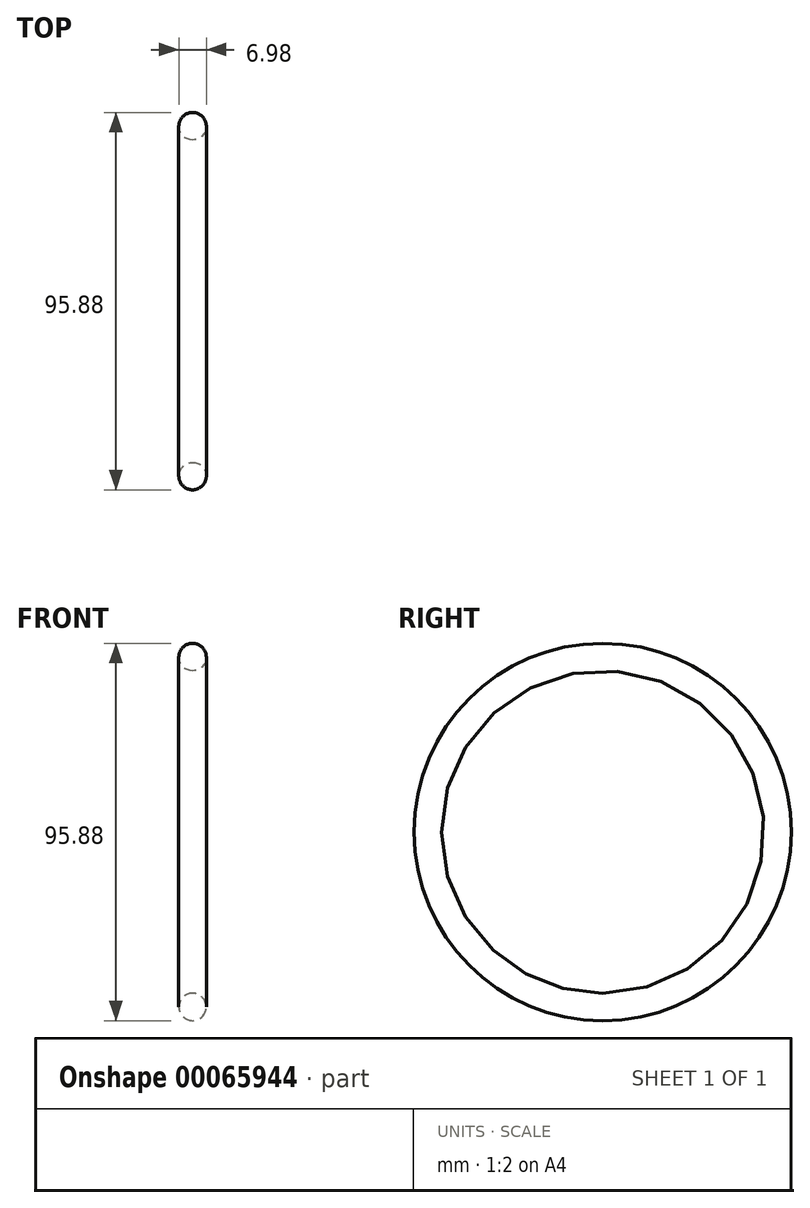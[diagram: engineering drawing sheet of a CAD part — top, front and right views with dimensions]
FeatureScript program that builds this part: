
annotation { "Feature Type Name" : "Feature", "Feature Type Description" : "" }
export const myFeature = defineFeature(function(context is Context, id is Id, definition is map)
    precondition{}
    {
        {
            var Q0;
            Q0=qCreatedBy(makeId("Front.planeOp"),FACE);
            var sketch = newSketch(context, id + "F0", { "sketchPlane" : qUnion([Q0])});
            skLineSegment(sketch, "E0", {"start": v(0, 0) * mm, "end": v(-6.06, 0) * mm, "construction": true});
            skCircle(sketch, "E1", {"center": v(0, 44.45) * mm, "radius": 3.5 * mm});
            skSolve(sketch);
        }
        {
            var Q0;
            Q0=makeQuery(id+"F0.imprint","IMPRINT",FACE,{"disambiguationData":[TD([[makeQuery(id+"F0.imprint","IMPRINT",EDGE,{"derivedFrom":sQuery(id+"F0.wireOp",EDGE,"E1")}),1.0]])]});
            var Q1;
            Q1=sQuery(id+"F0.wireOp",EDGE,"E0");
            revolve(context, id + "F1", {"entities" : qUnion([Q0]), "axis" : qUnion([Q1]), "revolveType" : RevolveType.FULL});
        }
    });
